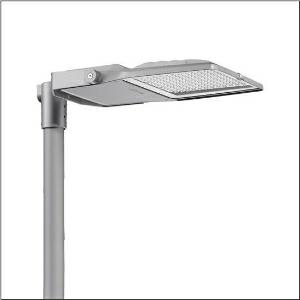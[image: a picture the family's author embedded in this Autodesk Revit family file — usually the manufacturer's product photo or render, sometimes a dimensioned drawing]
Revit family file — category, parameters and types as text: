
# Revit family: floodlight_fl_21_midi___pl52_5xa7785f2d3a_eb33
name_source: partatom
category: Lighting Fixtures
units: mm (PartAtom-declared; Revit-internal decimal feet)

## family parameters
Cut with Voids When Loaded = No
Host = Face
Light Source = No
Part Type = Normal
Room Calculation Point = No
Round Connector Dimension = Use Diameter
Shared = No

## types (1)
- --- (1 x LED, 35750 lm, 271.6 W, 3000K)
    Apparent Load = 272 VA
    CIE Flux Codes = 26 60 98 100 100
    Color Rendering = 70
    Color Temperature = 3000K
    Default Elevation = 1800 mm
    Description = Floodlight FL 21 midi, floodlight, primary light control with lens, of PMMA, primary optical cover: protective disc, of toughened safety glass, transparent, light distribution: PL52, light emission: direct distribution, installation type: surface-mounted, LED, High Power LED, rated luminous flux: 35.750lm, luminous efficacy: 132lm/W, light colour: 730, colour temperature: 3000K, control gear: Smart Interface (Zhaga), control: flexible luminous flux parameterisation, time-dependent luminous flux control, constant luminous flux control, overheat protection, pre-setting: logarithmic dimming characteristic, with terminal, 6-pole, mains connection: 220..240V, AC, 50/60Hz, start of lifetime: 272W, end of service life: 287W, reduction: 123W, luminaire housing, of diecast aluminium, powder-coated, SITECO metallic grey (DB 702S), corrosivity category C5 mid according to DIN EN ISO 12944, suitable for swimming pools, chlorine-resistant, sealing non-destructively replaceable, please order mast flange separately, mast bracket, of steel, galvanised, powder-coated, SITECO metallic grey (DB 702S), Smart Interface above, protection rating (complete): IP66, insulation class (complete): insulation class II (safety insulation), certification: CE, ENEC, VDE, protection symbol: D, impact resistance: IK08, permissible operating ambient temperature: -40..+40°C, permissible operating ambient temperature for outdoor applications: -40..+50°C, standard: DIN EN 12944, LABS conformity tested according to VDMA 24364:2018-05, packaging unit: 1 piece

Light Distribution: PL52
    Height = 76 mm
    Lamp = 1 x LED
    Lamp Light Flux = 35750 lm
    Lamp Power = 271.6 W
    Lamp count = 1
    Length = 657 mm
    Luminous efficacy = 132 lm/W
    Manufacturer = Siteco
    ModVariant = No
    Model = 5XA7785F2D3A
    Number of Poles = 1
    OnlyDefault = Yes
    Power Factor = 1
    Product Name = Floodlight FL 21 midi | PL52
    Product group = floodlight | pylon annexe
    ProductGroupID = 6201
    Protection Class = Protection class II
    Protection Degree = IP 66
    RLX_Detail_Level = 1
    RLX_Emergency_Light_Flux = 0 lm
    RLX_Emergency_Type = 0
    RLX_Emergency_Type_DB = No
    RlxData = <blob elided: 154049 chars, md5=2223230f>
    Socket = socket
    Standby Power = 0 W
    System Light Flux = 35750 lm
    System Power = 272 W
    Type Comments = factory setting: luminous flux: 100 % | dim-lin: 254 | 620 mA
    Type Image = l_1007123.jpg
    URL = http://relux.com
    VarID = @adj_176959
    Voltage = 0 V
    Weight = 0.00 kg
    Width = 442 mm

## geometry (parser evidence)
native form markers: Blend x4, Sweep x15
no freeform markers — native parametric forms only
